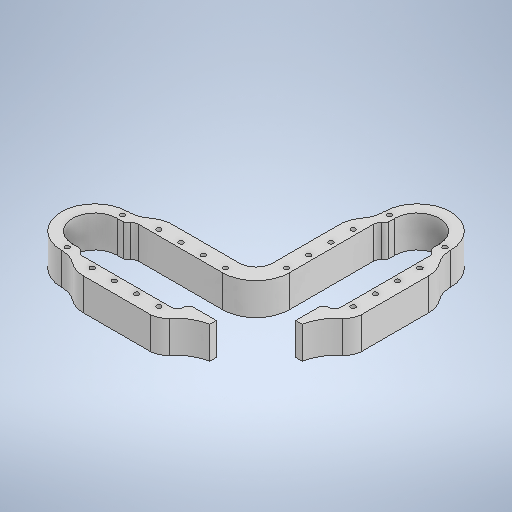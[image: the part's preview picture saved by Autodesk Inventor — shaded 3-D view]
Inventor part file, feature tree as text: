
AUTODESK INVENTOR PART (.ipt)
format: ipt  version: 2025.1 (Build 291241020, 241B)  size: 742,912 bytes
history: native  units: in
note: dims shown in document units (in); Inventor stores cm internally (conversion verified against a paired STEP export)
features: extrude x7, sketch x6, projected_geometry x5, fillet x4
ambient origin geometry x8: Origin, YZ Plane, XZ Plane, XY Plane, X Axis, Y Axis, Z Axis, Center Point
bodies: Solid1 (feature_tree)
feature tree (22):
  sketch  "Sketch1"  dims[d1=1.5in d2=1.5in d3=1.0in d4=1.0in d6=0.75in]
  extrude  "Extrusion1"  Depth=1.5in
  fillet  "Fillet1"  Radius=1.0in
  fillet  "Fillet2"  Radius=1.0in
  fillet  "Fillet4"  Radius=0.75in
  extrude  "Extrusion2"  Depth=0.75in
  fillet  "Fillet5"  Radius=1.0in
  extrude  "Extrusion3"  Depth=4.0in
  extrude  "Extrusion4"  Depth=0.75in
  extrude  "Extrusion5"  Depth=0.5in
  extrude  "Extrusion6"  Depth=0.25in
  extrude  "Extrusion7"  Depth=0.25in
  sketch  "Sketch2"  dims[d7=0.75in d8=0.75in d9=1.0in]
  projected_geometry  "Projected Loop1"
  sketch  "Sketch3"  dims[d10=4.0in d11=4.0in]
  projected_geometry  "Projected Loop2"
  sketch  "Sketch4"  dims[d17=0.75in d18=0.75in]
  projected_geometry  "Projected Loop3"
  sketch  "Sketch5"  dims[d19=0.5in d23=0.5in]
  projected_geometry  "Projected Loop4"
  sketch  "Sketch6"  dims[d24=0.75in d25=0.75in d30=0.5in d33=0.25in d47=0.75in d48=0.75in d49=0.5in d50=0.5in d51=1.0in d52=4.875in d53=5.2441in d54=5.2441in d55=0.4522in d56=0.4522in d57=2.0in d58=4.875in d59=2.0in d60=4.5in d61=4.5in d62=0.5in d63=0.5in d64=0.75in d65=0.75in d66=0.5in d70=4.9941in d71=1.355in d72=0.0in d73=2.0in d74=0.75in d76=1.5in d77=1.355in d78=0.0in d79=0.25in d80=0.2087in d81=1.0in d82=1.0in d83=1.0in d84=1.0in d85=1.0in d86=1.0in d87=1.0in d88=1.0in d89=1.0in d90=1.0in d91=1.0in d92=1.0in d93=1.25in d94=1.25in d95=1.25in d96=1.25in d97=3.0in d98=1.5in d99=3.0in d100=1.5in d101=1.375in d102=1.375in d103=1.375in d104=1.375in d105=0.0in d106=0.0in d108=1.2584in d109=1.2584in d110=0.0in d111=0.0in d112=0.025in d113=0.0in d114=0.06in d115=0.0in d116=2.625in d117=0.0in]
  projected_geometry  "Projected Loop5"
